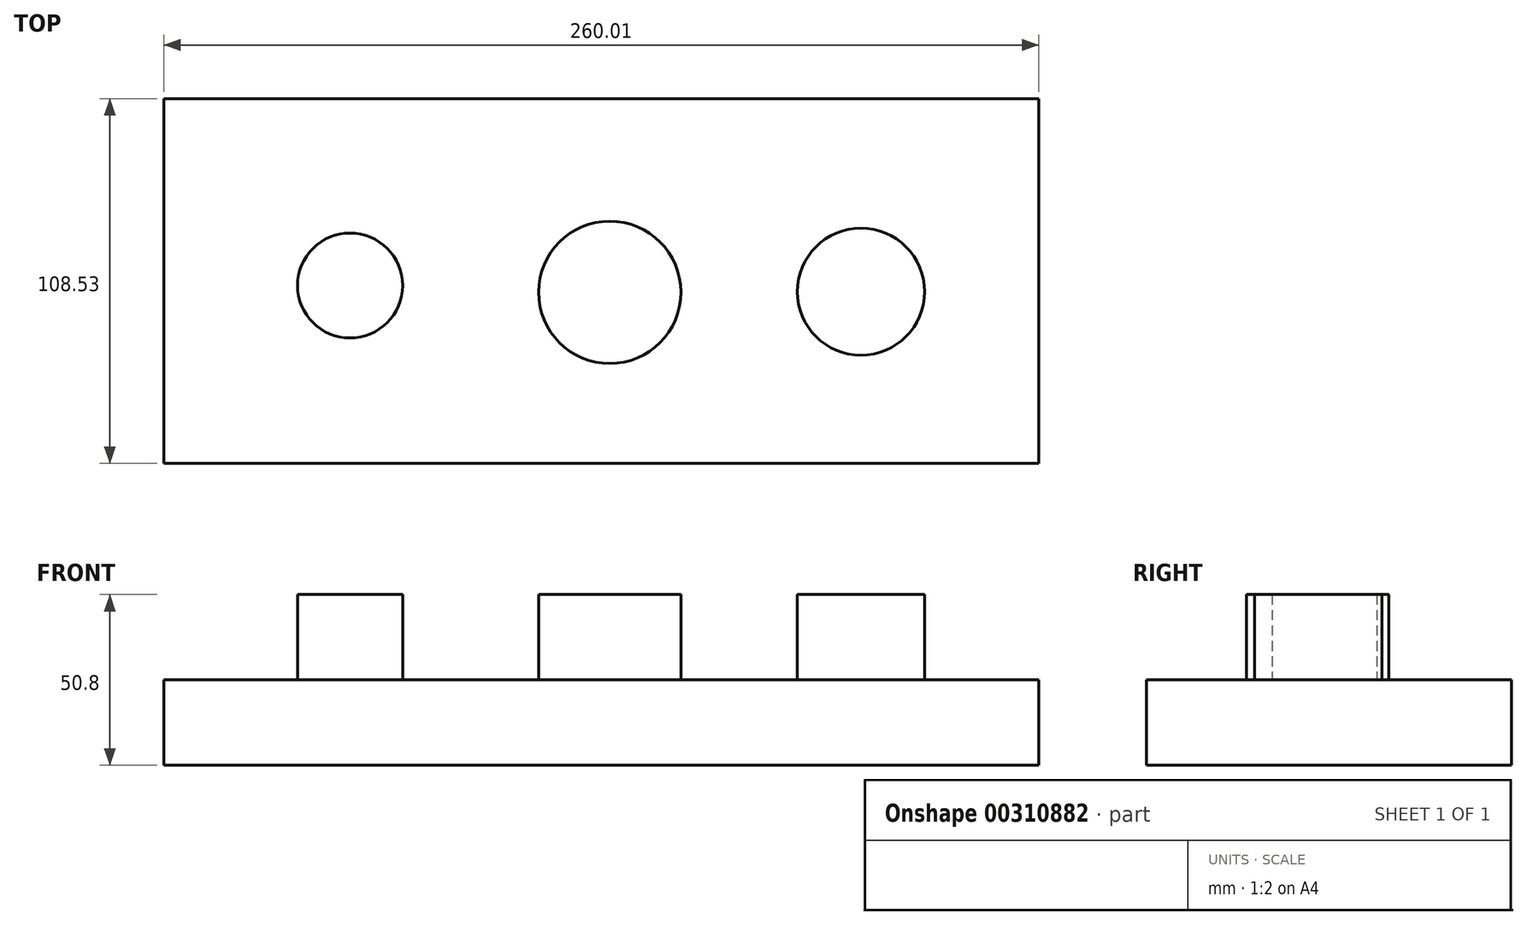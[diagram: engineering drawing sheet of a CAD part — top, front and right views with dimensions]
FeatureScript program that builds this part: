
annotation { "Feature Type Name" : "Feature", "Feature Type Description" : "" }
export const myFeature = defineFeature(function(context is Context, id is Id, definition is map)
    precondition{}
    {
        {
            var Q0;
            Q0=qCreatedBy(makeId("Top.planeOp"),FACE);
            var sketch = newSketch(context, id + "F0", { "sketchPlane" : qUnion([Q0])});
            skLineSegment(sketch, "E0.bottom", {"start": v(-124.02, 41.78) * mm, "end": v(135.99, 41.78) * mm});
            skLineSegment(sketch, "E0.top", {"start": v(-124.02, -66.75) * mm, "end": v(135.99, -66.75) * mm});
            skLineSegment(sketch, "E0.left", {"start": v(-124.02, 41.78) * mm, "end": v(-124.02, -66.75) * mm});
            skLineSegment(sketch, "E0.right", {"start": v(135.99, 41.78) * mm, "end": v(135.99, -66.75) * mm});
            skSolve(sketch);
        }
        {
            var Q0;
            Q0=makeQuery(id+"F0.imprint","IMPRINT",FACE,{"disambiguationData":[TD([[makeQuery(id+"F0.imprint","IMPRINT",EDGE,{"derivedFrom":sQuery(id+"F0.wireOp",EDGE,"E0.bottom")}),-1.0]])]});
            extrude(context, id + "F1", {"entities" : qUnion([Q0]), "depth" : 25.4 * mm});
        }
        {
            var Q0;
            Q0=makeQuery(id+"F1.opExtrude","CAP_FACE",FACE,{"disambiguationData":[OSD([sQuery(id+"F0.wireOp",EDGE,"E0.bottom"),sQuery(id+"F0.wireOp",EDGE,"E0.top"),sQuery(id+"F0.wireOp",EDGE,"E0.left"),sQuery(id+"F0.wireOp",EDGE,"E0.right")])],"isStart":false});
            var sketch = newSketch(context, id + "F2", { "sketchPlane" : qUnion([Q0])});
            skCircle(sketch, "E1", {"center": v(-68.63, -13.82) * mm, "radius": 15.61 * mm});
            skCircle(sketch, "E2", {"center": v(8.54, -15.85) * mm, "radius": 21.15 * mm});
            skCircle(sketch, "E3", {"center": v(83.2, -15.65) * mm, "radius": 18.9 * mm});
            skSolve(sketch);
        }
        {
            var Q0;
            Q0 = qSketchRegion(id + "F2", true);
            extrude(context, id + "F3", {"entities" : qUnion([Q0]), "operationType" : NewBodyOperationType.ADD, "depth" : 25.4 * mm});
        }
    });
